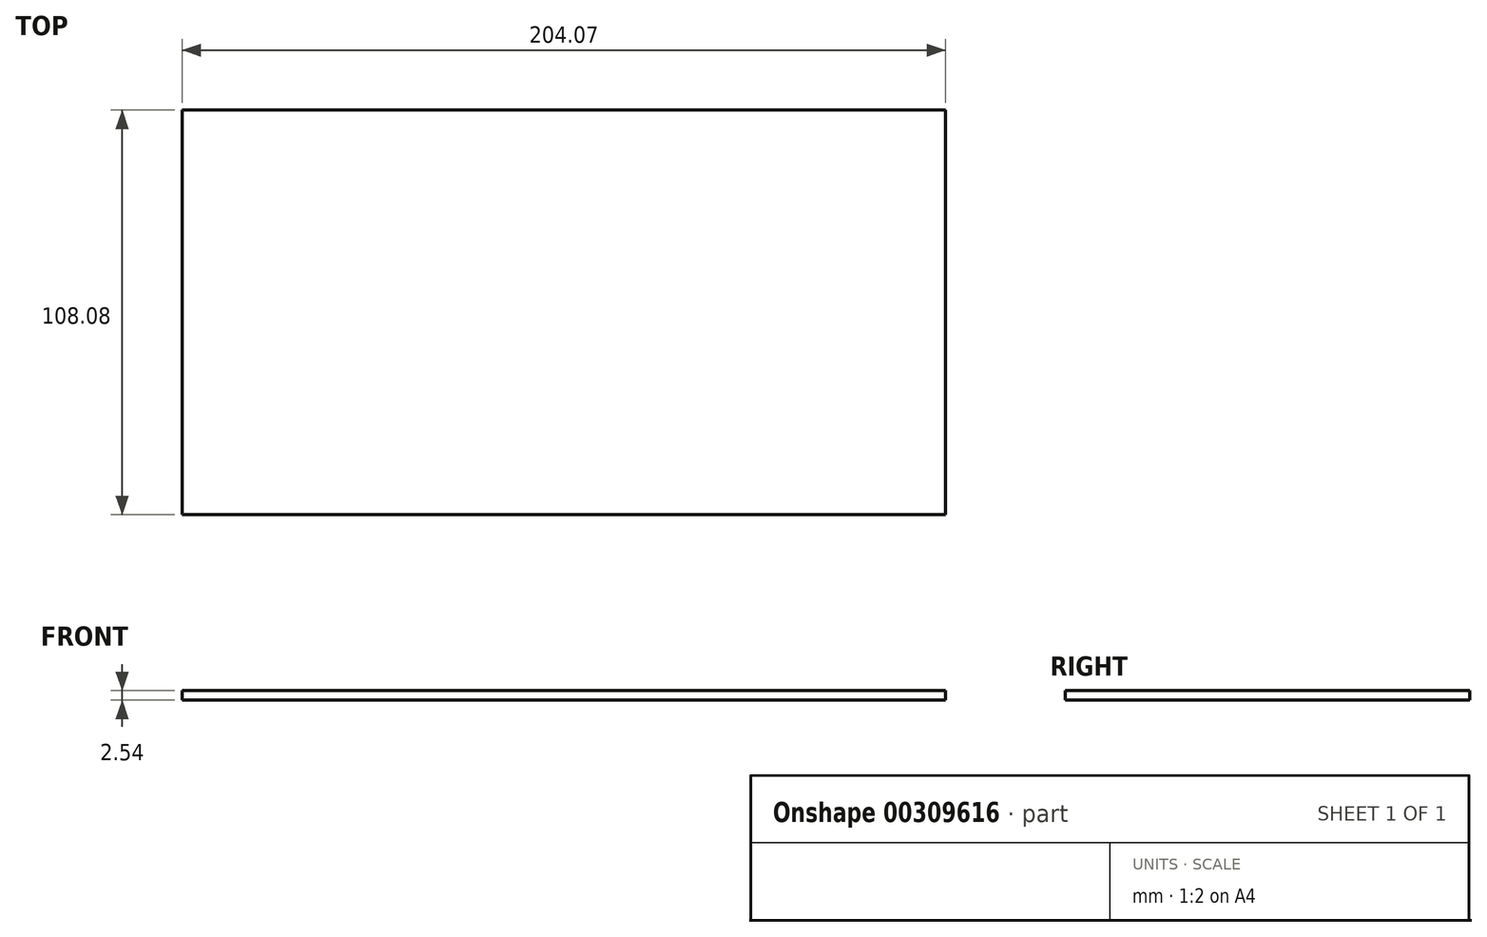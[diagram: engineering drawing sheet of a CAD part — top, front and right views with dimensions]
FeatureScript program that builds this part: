
annotation { "Feature Type Name" : "Feature", "Feature Type Description" : "" }
export const myFeature = defineFeature(function(context is Context, id is Id, definition is map)
    precondition{}
    {
        {
            var Q0;
            Q0=qCreatedBy(makeId("Top.planeOp"),FACE);
            var sketch = newSketch(context, id + "F0", { "sketchPlane" : qUnion([Q0])});
            skLineSegment(sketch, "E0.bottom", {"start": v(-128.4, 32.15) * mm, "end": v(75.68, 32.15) * mm});
            skLineSegment(sketch, "E0.top", {"start": v(-128.4, -75.93) * mm, "end": v(75.68, -75.93) * mm});
            skLineSegment(sketch, "E0.left", {"start": v(-128.4, 32.15) * mm, "end": v(-128.4, -75.93) * mm});
            skLineSegment(sketch, "E0.right", {"start": v(75.68, 32.15) * mm, "end": v(75.68, -75.93) * mm});
            skLineSegment(sketch, "E1.bottom", {"start": v(0, 32.15) * mm, "end": v(0, 32.15) * mm});
            skLineSegment(sketch, "E1.top", {"start": v(0, 85.19) * mm, "end": v(0, 85.19) * mm});
            skLineSegment(sketch, "E1.left", {"start": v(0, 32.15) * mm, "end": v(0, 85.19) * mm});
            skLineSegment(sketch, "E1.right", {"start": v(0, 32.15) * mm, "end": v(0, 85.19) * mm});
            skSolve(sketch);
        }
        {
            var Q0;
            Q0=makeQuery(id+"F0.imprint","IMPRINT",FACE,{"disambiguationData":[TD([[makeQuery(id+"F0.imprint","IMPRINT",EDGE,{"derivedFrom":sQuery(id+"F0.wireOp",EDGE,"E0.top")}),1.0]])]});
            var Q1;
            Q1=sQuery(id+"F0.wireOp",EDGE,"E1.right");
            var Q2;
            Q2=sQuery(id+"F0.wireOp",EDGE,"E1.left");
            extrude(context, id + "F1", {"entities" : qUnion([Q0]), "surfaceEntities" : qUnion([Q1, Q2]), "depth" : 2.54 * mm});
        }
    });
